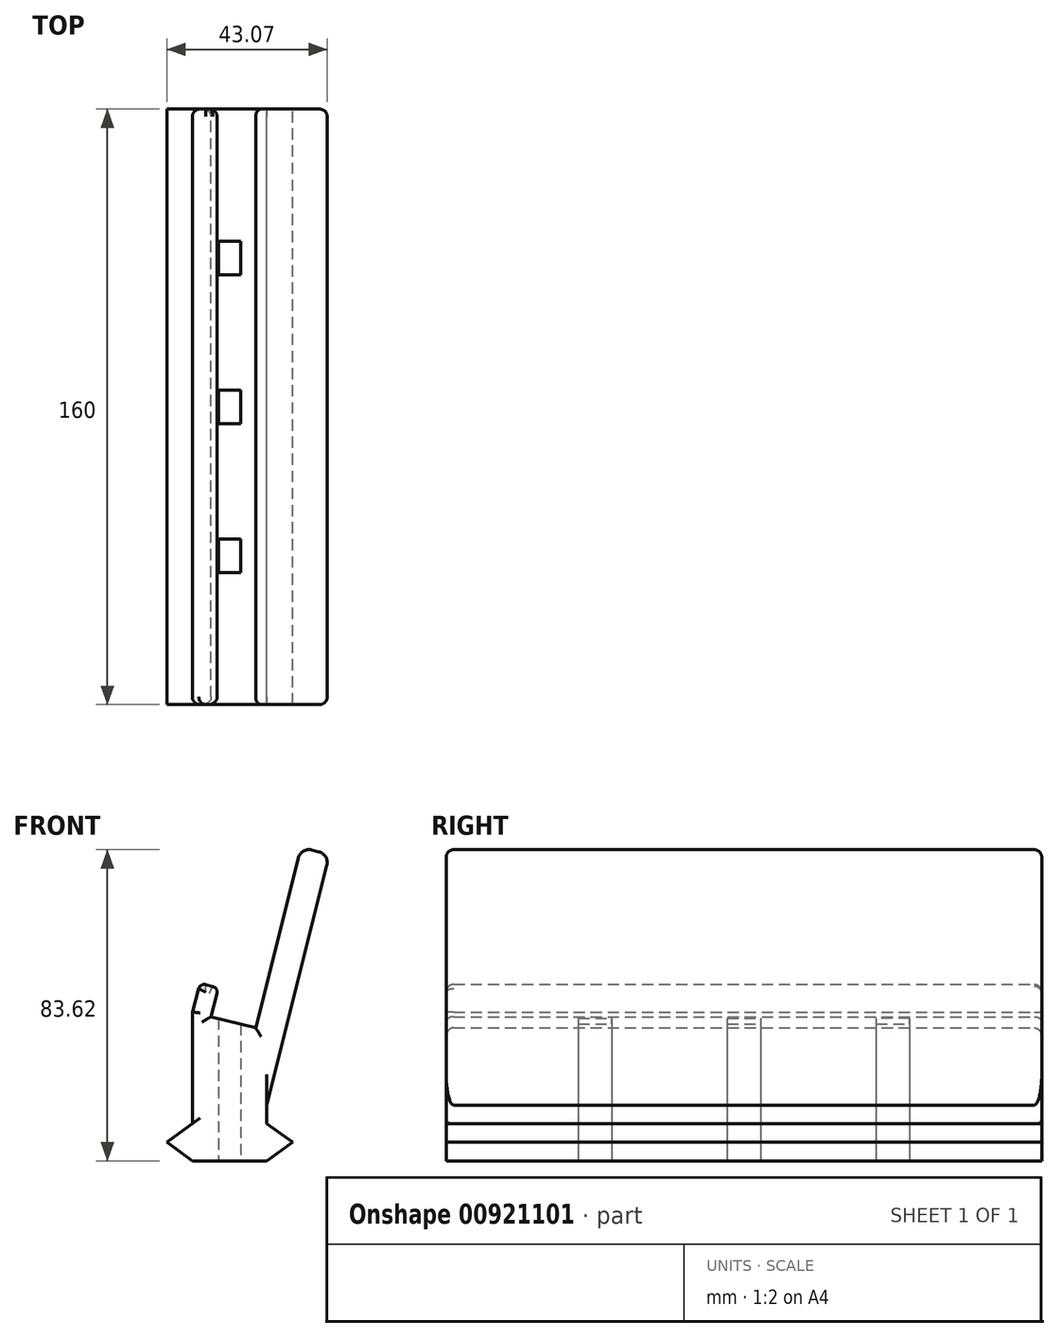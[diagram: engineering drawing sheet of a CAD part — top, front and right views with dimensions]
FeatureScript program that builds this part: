
annotation { "Feature Type Name" : "Feature", "Feature Type Description" : "" }
export const myFeature = defineFeature(function(context is Context, id is Id, definition is map)
    precondition{}
    {
        {
            var Q0;
            Q0=qCreatedBy(makeId("Front.planeOp"),FACE);
            var sketch = newSketch(context, id + "F0", { "sketchPlane" : qUnion([Q0])});
            skLineSegment(sketch, "E0", {"start": v(-25.55, 13.75) * mm, "end": v(-5.55, 13.75) * mm});
            skLineSegment(sketch, "E1", {"start": v(-25.55, 3.75) * mm, "end": v(-5.55, 3.75) * mm});
            skLineSegment(sketch, "E2", {"start": v(-25.55, 13.75) * mm, "end": v(-32.43, 8.75) * mm});
            skLineSegment(sketch, "E3", {"start": v(-32.43, 8.75) * mm, "end": v(-25.55, 3.75) * mm});
            skLineSegment(sketch, "E4", {"start": v(-5.55, 13.75) * mm, "end": v(1.32, 8.75) * mm});
            skLineSegment(sketch, "E5", {"start": v(1.32, 8.75) * mm, "end": v(-5.55, 3.75) * mm});
            skLineSegment(sketch, "E6", {"start": v(-25.55, 13.75) * mm, "end": v(-25.55, 43.75) * mm});
            skLineSegment(sketch, "E7", {"start": v(-5.55, 13.75) * mm, "end": v(-5.55, 38.75) * mm});
            skLineSegment(sketch, "E8", {"start": v(-5.55, 38.75) * mm, "end": v(-25.55, 43.75) * mm});
            skPoint(sketch, "E9", {"position": v(-8.55, 39.5) * mm});
            skPoint(sketch, "E10", {"position": v(-20.55, 42.5) * mm});
            skLineSegment(sketch, "E11", {"start": v(-8.55, 39.5) * mm, "end": v(2.85, 85.1) * mm});
            skPoint(sketch, "E12", {"position": v(-5.55, 18.75) * mm});
            skLineSegment(sketch, "E13", {"start": v(-5.55, 18.75) * mm, "end": v(10.55, 83.17) * mm});
            skLineSegment(sketch, "E14", {"start": v(6.48, 87.28) * mm, "end": v(8.37, 86.8) * mm});
            skLineSegment(sketch, "E15", {"start": v(-20.55, 42.5) * mm, "end": v(-18.98, 48.8) * mm});
            skLineSegment(sketch, "E16", {"start": v(-20.07, 50.62) * mm, "end": v(-22.04, 51.11) * mm});
            skLineSegment(sketch, "E17", {"start": v(-25.55, 43.75) * mm, "end": v(-23.85, 50.05) * mm});
            skPoint(sketch, "E18.visualSharp", {"position": v(11.28, 86.08) * mm});
            skArc(sketch, "E18.filletArc", {"start": v(10.55, 83.17) * mm, "mid": v(10.21, 85.44) * mm, "end": v(8.37, 86.8) * mm});
            skPoint(sketch, "E19.visualSharp", {"position": v(3.57, 88) * mm});
            skArc(sketch, "E19.filletArc", {"start": v(6.48, 87.28) * mm, "mid": v(4.21, 86.94) * mm, "end": v(2.85, 85.1) * mm});
            skPoint(sketch, "E20.visualSharp", {"position": v(-23.46, 51.47) * mm});
            skArc(sketch, "E20.filletArc", {"start": v(-22.04, 51.11) * mm, "mid": v(-23.16, 50.95) * mm, "end": v(-23.85, 50.05) * mm});
            skPoint(sketch, "E21.visualSharp", {"position": v(-18.61, 50.26) * mm});
            skArc(sketch, "E21.filletArc", {"start": v(-18.98, 48.8) * mm, "mid": v(-19.14, 49.94) * mm, "end": v(-20.07, 50.62) * mm});
            skSolve(sketch);
        }
        {
            var Q0;
            {var subQ4=sQuery(id+"F0.wireOp",EDGE,"E0");Q0=makeQuery(id+"F0.imprint","IMPRINT",FACE,{"disambiguationData":[TD([[makeQuery(id+"F0.imprint","IMPRINT",EDGE,{"derivedFrom":subQ4}),1.0]])]});}
            var Q1;
            {var subQ0=sQuery(id+"F0.wireOp",EDGE,"E11");Q1=makeQuery(id+"F0.imprint","IMPRINT",FACE,{"disambiguationData":[TD([[makeQuery(id+"F0.imprint","IMPRINT",EDGE,{"derivedFrom":subQ0}),-1.0]])]});}
            var Q2;
            {var subQ1=sQuery(id+"F0.wireOp",EDGE,"E15");Q2=makeQuery(id+"F0.imprint","IMPRINT",FACE,{"disambiguationData":[TD([[makeQuery(id+"F0.imprint","IMPRINT",EDGE,{"derivedFrom":subQ1}),1.0]])]});}
            var Q3;
            Q3=makeQuery(id+"F0.imprint","IMPRINT",FACE,{"disambiguationData":[TD([[makeQuery(id+"F0.imprint","IMPRINT",EDGE,{"derivedFrom":sQuery(id+"F0.wireOp",EDGE,"E0")}),-1.0]])]});
            extrude(context, id + "F1", {"entities" : qUnion([Q0, Q1, Q2, Q3]), "depth" : 160 * mm, "offsetDistance" : 25 * mm});
        }
        {
            var Q0;
            Q0=qCreatedBy(makeId("Top.planeOp"),FACE);
            var sketch = newSketch(context, id + "F2", { "sketchPlane" : qUnion([Q0])});
            skLineSegment(sketch, "E22", {"start": v(-18.55, -35.5) * mm, "end": v(-18.55, -44.5) * mm});
            skLineSegment(sketch, "E23", {"start": v(-18.55, -44.5) * mm, "end": v(-12.55, -44.5) * mm});
            skLineSegment(sketch, "E24", {"start": v(-12.55, -44.5) * mm, "end": v(-12.55, -35.5) * mm});
            skLineSegment(sketch, "E25", {"start": v(-12.55, -35.5) * mm, "end": v(-18.55, -35.5) * mm});
            skLineSegment(sketch, "E26", {"start": v(-18.55, -124.5) * mm, "end": v(-12.55, -124.5) * mm});
            skLineSegment(sketch, "E27", {"start": v(-12.55, -124.5) * mm, "end": v(-12.55, -115.5) * mm});
            skLineSegment(sketch, "E28", {"start": v(-12.55, -115.5) * mm, "end": v(-18.55, -115.5) * mm});
            skLineSegment(sketch, "E29", {"start": v(-18.55, -124.5) * mm, "end": v(-18.55, -115.5) * mm});
            skLineSegment(sketch, "E30", {"start": v(-18.55, -84.5) * mm, "end": v(-18.55, -75.5) * mm});
            skLineSegment(sketch, "E31", {"start": v(-18.55, -75.5) * mm, "end": v(-12.55, -75.5) * mm});
            skLineSegment(sketch, "E32", {"start": v(-18.55, -84.5) * mm, "end": v(-12.55, -84.5) * mm});
            skLineSegment(sketch, "E33", {"start": v(-12.55, -84.5) * mm, "end": v(-12.55, -75.5) * mm});
            skSolve(sketch);
        }
        {
            var Q0;
            Q0=makeQuery(id+"F2.imprint","IMPRINT",FACE,{"disambiguationData":[TD([[makeQuery(id+"F2.imprint","IMPRINT",EDGE,{"derivedFrom":sQuery(id+"F2.wireOp",EDGE,"E22")}),1.0]])]});
            var Q1;
            Q1=makeQuery(id+"F2.imprint","IMPRINT",FACE,{"disambiguationData":[TD([[makeQuery(id+"F2.imprint","IMPRINT",EDGE,{"derivedFrom":sQuery(id+"F2.wireOp",EDGE,"E26")}),1.0]])]});
            var Q2;
            Q2=makeQuery(id+"F2.imprint","IMPRINT",FACE,{"disambiguationData":[TD([[makeQuery(id+"F2.imprint","IMPRINT",EDGE,{"derivedFrom":sQuery(id+"F2.wireOp",EDGE,"E30")}),-1.0]])]});
            extrude(context, id + "F3", {"entities" : qUnion([Q0, Q1, Q2]), "operationType" : NewBodyOperationType.REMOVE, "depth" : 42.5 * mm, "offsetDistance" : 25 * mm});
        }
        {
            var Q0;
            Q0=makeQuery(id+"F1.opExtrude","CAP_EDGE",EDGE,{"disambiguationData":[OSD([sQuery(id+"F0.wireOp",EDGE,"E6")])],"isStart":false});
            var Q1;
            Q1=makeQuery(id+"F1.opExtrude","CAP_EDGE",EDGE,{"disambiguationData":[OSD([sQuery(id+"F0.wireOp",EDGE,"E13")])],"isStart":false});
            var Q2;
            Q2=makeQuery(id+"F1.opExtrude","CAP_EDGE",EDGE,{"disambiguationData":[OSD([sQuery(id+"F0.wireOp",EDGE,"E11")])],"isStart":false});
            var Q3;
            Q3=makeQuery(id+"F1.opExtrude","CAP_EDGE",EDGE,{"disambiguationData":[OSD([sQuery(id+"F0.wireOp",EDGE,"E8")])],"isStart":false});
            var Q4;
            Q4=makeQuery(id+"F1.opExtrude","CAP_EDGE",EDGE,{"disambiguationData":[OSD([sQuery(id+"F0.wireOp",EDGE,"E15")])],"isStart":false});
            var Q5;
            Q5=makeQuery(id+"F1.opExtrude","CAP_EDGE",EDGE,{"disambiguationData":[OSD([sQuery(id+"F0.wireOp",EDGE,"E13")])],"isStart":true});
            var Q6;
            Q6=makeQuery(id+"F1.opExtrude","CAP_EDGE",EDGE,{"disambiguationData":[OSD([sQuery(id+"F0.wireOp",EDGE,"E11")])],"isStart":true});
            var Q7;
            Q7=makeQuery(id+"F1.opExtrude","CAP_EDGE",EDGE,{"disambiguationData":[OSD([sQuery(id+"F0.wireOp",EDGE,"E8")])],"isStart":true});
            var Q8;
            Q8=makeQuery(id+"F1.opExtrude","CAP_EDGE",EDGE,{"disambiguationData":[OSD([sQuery(id+"F0.wireOp",EDGE,"E15")])],"isStart":true});
            var Q9;
            Q9=makeQuery(id+"F1.opExtrude","CAP_EDGE",EDGE,{"disambiguationData":[OSD([sQuery(id+"F0.wireOp",EDGE,"E6")])],"isStart":true});
            fillet(context, id + "F4", {"entities" : qUnion([Q0, Q1, Q2, Q3, Q4, Q5, Q6, Q7, Q8, Q9]), "radius" : 2 * mm, "tangentPropagation" : true, "allowEdgeOverflow" : false});
        }
    });
